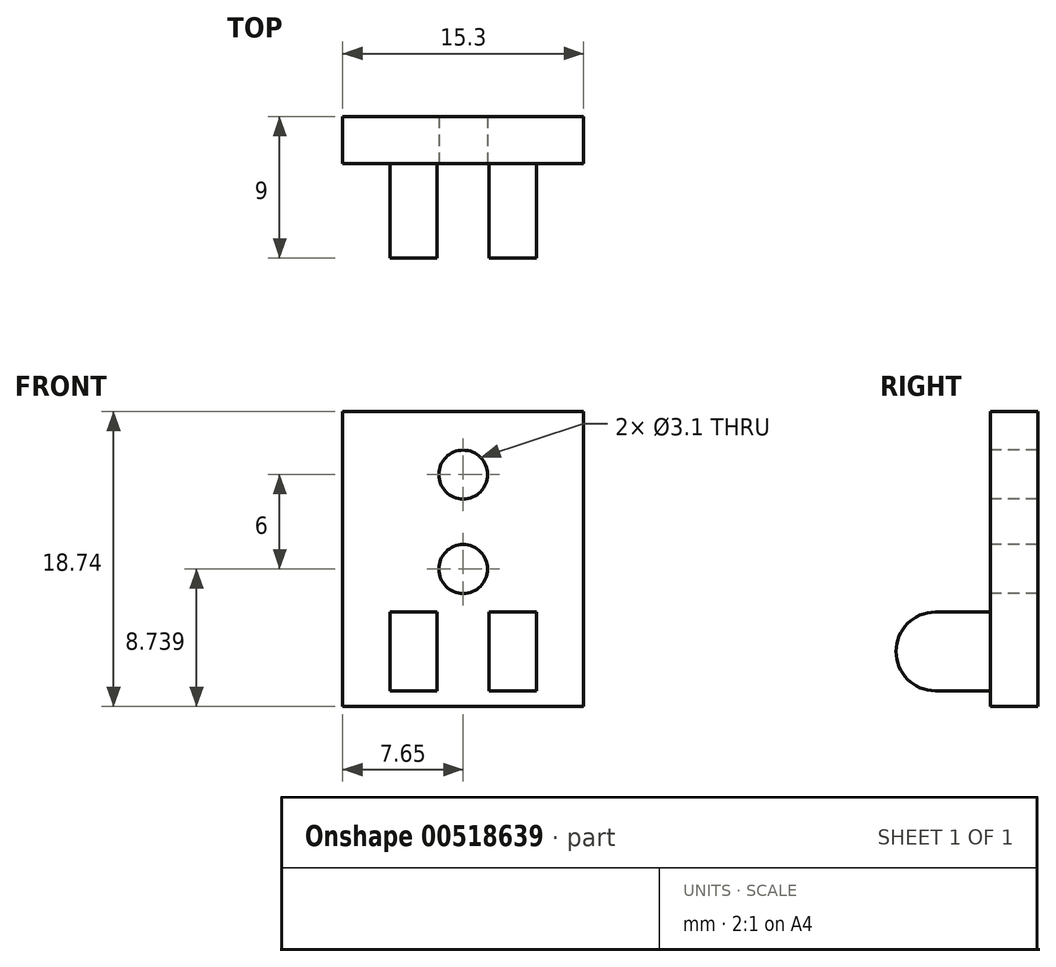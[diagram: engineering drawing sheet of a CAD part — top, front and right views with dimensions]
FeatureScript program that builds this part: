
annotation { "Feature Type Name" : "Feature", "Feature Type Description" : "" }
export const myFeature = defineFeature(function(context is Context, id is Id, definition is map)
    precondition{}
    {
        {
            var Q0;
            Q0=qCreatedBy(makeId("Front.planeOp"),FACE);
            var sketch = newSketch(context, id + "F0", { "sketchPlane" : qUnion([Q0])});
            skLineSegment(sketch, "E0.bottom", {"start": v(-7.65, 9.37) * mm, "end": v(7.65, 9.37) * mm});
            skLineSegment(sketch, "E0.top", {"start": v(-7.65, -9.37) * mm, "end": v(7.65, -9.37) * mm});
            skLineSegment(sketch, "E0.left", {"start": v(-7.65, 9.37) * mm, "end": v(-7.65, -9.37) * mm});
            skLineSegment(sketch, "E0.right", {"start": v(7.65, 9.37) * mm, "end": v(7.65, -9.37) * mm});
            skSolve(sketch);
        }
        {
            var Q0;
            Q0=makeQuery(id+"F0.imprint","IMPRINT",FACE,{"disambiguationData":[TD([[makeQuery(id+"F0.imprint","IMPRINT",EDGE,{"derivedFrom":sQuery(id+"F0.wireOp",EDGE,"E0.bottom")}),-1.0]])]});
            extrude(context, id + "F1", {"entities" : qUnion([Q0]), "depth" : 3 * mm, "offsetDistance" : 25 * mm});
        }
        {
            var Q0;
            Q0=makeQuery(id+"F1.opExtrude","CAP_FACE",FACE,{"disambiguationData":[OSD([sQuery(id+"F0.wireOp",EDGE,"E0.bottom"),sQuery(id+"F0.wireOp",EDGE,"E0.top"),sQuery(id+"F0.wireOp",EDGE,"E0.left"),sQuery(id+"F0.wireOp",EDGE,"E0.right")])],"isStart":false});
            var sketch = newSketch(context, id + "F2", { "sketchPlane" : qUnion([Q0])});
            skLineSegment(sketch, "E1.left", {"start": v(-4.65, -3.37) * mm, "end": v(-4.65, -8.37) * mm});
            skLineSegment(sketch, "E1.right", {"start": v(1.65, -3.37) * mm, "end": v(1.65, -8.37) * mm});
            skLineSegment(sketch, "E2.left", {"start": v(-1.65, -3.37) * mm, "end": v(-1.65, -8.37) * mm});
            skLineSegment(sketch, "E2.right", {"start": v(4.65, -3.37) * mm, "end": v(4.65, -8.37) * mm});
            skLineSegment(sketch, "E3", {"start": v(-4.65, -3.37) * mm, "end": v(-1.65, -3.37) * mm});
            skLineSegment(sketch, "E4", {"start": v(1.65, -3.37) * mm, "end": v(4.65, -3.37) * mm});
            skLineSegment(sketch, "E5", {"start": v(-4.65, -8.37) * mm, "end": v(-1.65, -8.37) * mm});
            skLineSegment(sketch, "E6", {"start": v(1.65, -8.37) * mm, "end": v(4.65, -8.37) * mm});
            skSolve(sketch);
        }
        {
            var Q0;
            Q0=makeQuery(id+"F2.imprint","IMPRINT",FACE,{"disambiguationData":[TD([[makeQuery(id+"F2.imprint","IMPRINT",EDGE,{"derivedFrom":sQuery(id+"F2.wireOp",EDGE,"E1.left")}),1.0]])]});
            var Q1;
            Q1=makeQuery(id+"F2.imprint","IMPRINT",FACE,{"disambiguationData":[TD([[makeQuery(id+"F2.imprint","IMPRINT",EDGE,{"derivedFrom":sQuery(id+"F2.wireOp",EDGE,"E1.right")}),1.0]])]});
            extrude(context, id + "F3", {"entities" : qUnion([Q0, Q1]), "operationType" : NewBodyOperationType.ADD, "depth" : 3.5 * mm, "offsetDistance" : 25 * mm});
        }
        {
            var Q0;
            Q0=makeQuery(id+"F3.opExtrude","SWEPT_FACE",FACE,{"disambiguationData":[OSD([sQuery(id+"F2.wireOp",EDGE,"E1.left")])]});
            var sketch = newSketch(context, id + "F4", { "sketchPlane" : qUnion([Q0])});
            skCircle(sketch, "E7", {"center": v(6.5, -5.87) * mm, "radius": 2.5 * mm});
            skSolve(sketch);
        }
        {
            var Q0;
            Q0=makeQuery(id+"F1.opExtrude","CAP_FACE",FACE,{"disambiguationData":[OSD([sQuery(id+"F0.wireOp",EDGE,"E0.bottom"),sQuery(id+"F0.wireOp",EDGE,"E0.top"),sQuery(id+"F0.wireOp",EDGE,"E0.left"),sQuery(id+"F0.wireOp",EDGE,"E0.right")])],"isStart":false});
            var sketch = newSketch(context, id + "F5", { "sketchPlane" : qUnion([Q0])});
            skCircle(sketch, "E8", {"center": v(0, -0.63) * mm, "radius": 1.55 * mm});
            skCircle(sketch, "E9", {"center": v(0, 5.37) * mm, "radius": 1.55 * mm});
            skSolve(sketch);
        }
        {
            var Q0;
            Q0 = qSketchRegion(id + "F5", true);
            extrude(context, id + "F6", {"entities" : qUnion([Q0]), "operationType" : NewBodyOperationType.REMOVE, "oppositeDirection" : true, "depth" : 5 * mm, "offsetDistance" : 25 * mm});
        }
        {
            var Q0;
            {var subQ1=sQuery(id+"F2.wireOp",EDGE,"E1.left");var subQ2=makeQuery(id+"F3.opExtrude","CAP_EDGE",EDGE,{"disambiguationData":[OSD([subQ1])],"isStart":false});Q0=makeQuery(id+"F4.imprint","IMPRINT",FACE,{"disambiguationData":[TD([[makeQuery(id+"F4.imprint","IMPRINT",EDGE,{"derivedFrom":subQ2}),1.0]])]});}
            extrude(context, id + "F7", {"entities" : qUnion([Q0]), "operationType" : NewBodyOperationType.ADD, "oppositeDirection" : true, "depth" : 3 * mm, "offsetDistance" : 25 * mm});
        }
        {
            var Q0;
            Q0=makeQuery(id+"F3.opExtrude","SWEPT_FACE",FACE,{"disambiguationData":[OSD([sQuery(id+"F2.wireOp",EDGE,"E2.right")])]});
            var sketch = newSketch(context, id + "F8", { "sketchPlane" : qUnion([Q0])});
            skCircle(sketch, "E10", {"center": v(-6.5, -5.87) * mm, "radius": 2.5 * mm});
            skSolve(sketch);
        }
        {
            var Q0;
            {var subQ1=sQuery(id+"F2.wireOp",EDGE,"E2.right");var subQ2=makeQuery(id+"F3.opExtrude","CAP_EDGE",EDGE,{"disambiguationData":[OSD([subQ1])],"isStart":false});Q0=makeQuery(id+"F8.imprint","IMPRINT",FACE,{"disambiguationData":[TD([[makeQuery(id+"F8.imprint","IMPRINT",EDGE,{"derivedFrom":subQ2}),1.0]])]});}
            var Q1;
            {var subQ1=sQuery(id+"F2.wireOp",EDGE,"E2.right");var subQ2=makeQuery(id+"F3.opExtrude","CAP_EDGE",EDGE,{"disambiguationData":[OSD([subQ1])],"isStart":false});Q1=makeQuery(id+"F8.imprint","IMPRINT",FACE,{"disambiguationData":[TD([[makeQuery(id+"F8.imprint","IMPRINT",EDGE,{"derivedFrom":subQ2}),-1.0]])]});}
            extrude(context, id + "F9", {"entities" : qUnion([Q0, Q1]), "operationType" : NewBodyOperationType.ADD, "oppositeDirection" : true, "depth" : 3 * mm, "offsetDistance" : 25 * mm});
        }
    });
